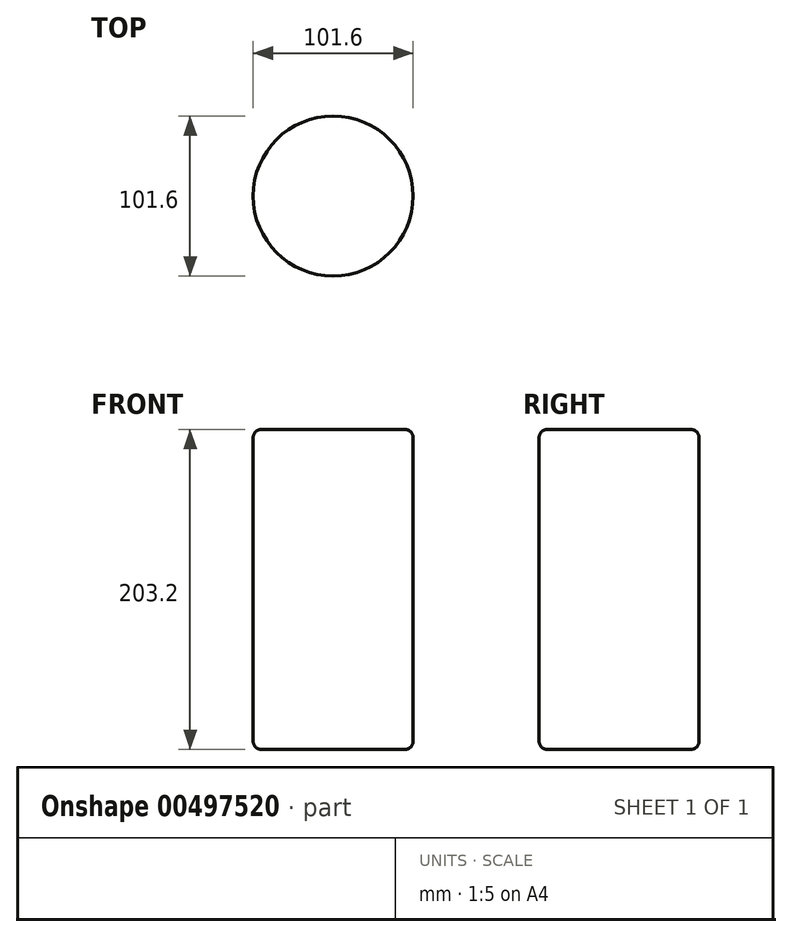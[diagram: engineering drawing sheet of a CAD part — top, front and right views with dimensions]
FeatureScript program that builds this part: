
annotation { "Feature Type Name" : "Feature", "Feature Type Description" : "" }
export const myFeature = defineFeature(function(context is Context, id is Id, definition is map)
    precondition{}
    {
        {
            var Q0;
            Q0=qCreatedBy(makeId("Top.planeOp"),FACE);
            var sketch = newSketch(context, id + "F0", { "sketchPlane" : qUnion([Q0])});
            skCircle(sketch, "E0", {"center": v(0, 0) * mm, "radius": 50.8 * mm});
            skSolve(sketch);
        }
        {
            var Q0;
            Q0=makeQuery(id+"F0.imprint","IMPRINT",FACE,{"disambiguationData":[TD([[makeQuery(id+"F0.imprint","IMPRINT",EDGE,{"derivedFrom":sQuery(id+"F0.wireOp",EDGE,"E0")}),1.0]])]});
            extrude(context, id + "F1", {"entities" : qUnion([Q0]), "depth" : 203.2 * mm});
        }
        {
            var Q0;
            Q0=makeQuery(id+"F1.opExtrude","CAP_FACE",FACE,{"disambiguationData":[OSD([sQuery(id+"F0.wireOp",EDGE,"E0")])],"isStart":true});
            var Q1;
            Q1=makeQuery(id+"F1.opExtrude","CAP_FACE",FACE,{"disambiguationData":[OSD([sQuery(id+"F0.wireOp",EDGE,"E0")])],"isStart":false});
            fillet(context, id + "F2", {"entities" : qUnion([Q0, Q1]), "radius" : 5.08 * mm, "tangentPropagation" : true, "allowEdgeOverflow" : false});
        }
    });
